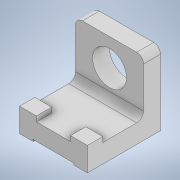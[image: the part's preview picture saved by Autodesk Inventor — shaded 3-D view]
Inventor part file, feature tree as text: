
AUTODESK INVENTOR PART (.ipt)
format: ipt  version: 2022.2 (Build 262287030, 287C)  size: 153,600 bytes
history: native  units: in
note: dims shown in document units (in); Inventor stores cm internally (conversion verified against a paired STEP export)
features: extrude x4, sketch x4, fillet x1
ambient origin geometry x8: Origin, YZ Plane, XZ Plane, XY Plane, X Axis, Y Axis, Z Axis, Center Point
bodies: Solid1 (feature_tree)
feature tree (9):
  extrude  "Extrusion1"  Depth=4.0in
  extrude  "Extrusion2"  Depth=5.375in
  extrude  "Extrusion3"  Depth=1.75in
  extrude  "Extrusion4"  Depth=4.125in TaperAngle=0.0deg
  fillet  "Fillet1"  Radius=0.125in
  sketch  "Sketch4"  dims[d2=5.0in d3=4.0in]
  sketch  "Sketch5"  dims[d4=2.5in d5=5.375in]
  sketch  "Sketch6"  dims[d6=1.25in d7=0.0in d8=1.75in]
  sketch  "Sketch7"  dims[d9=0.375in d10=4.125in d11=0.0in d12=0.125in d13=1.0in d14=3.0in d15=0.0in d16=0.0in d17=2.5in d18=3.0in d19=0.375in d20=0.0in d21=0.5in]
